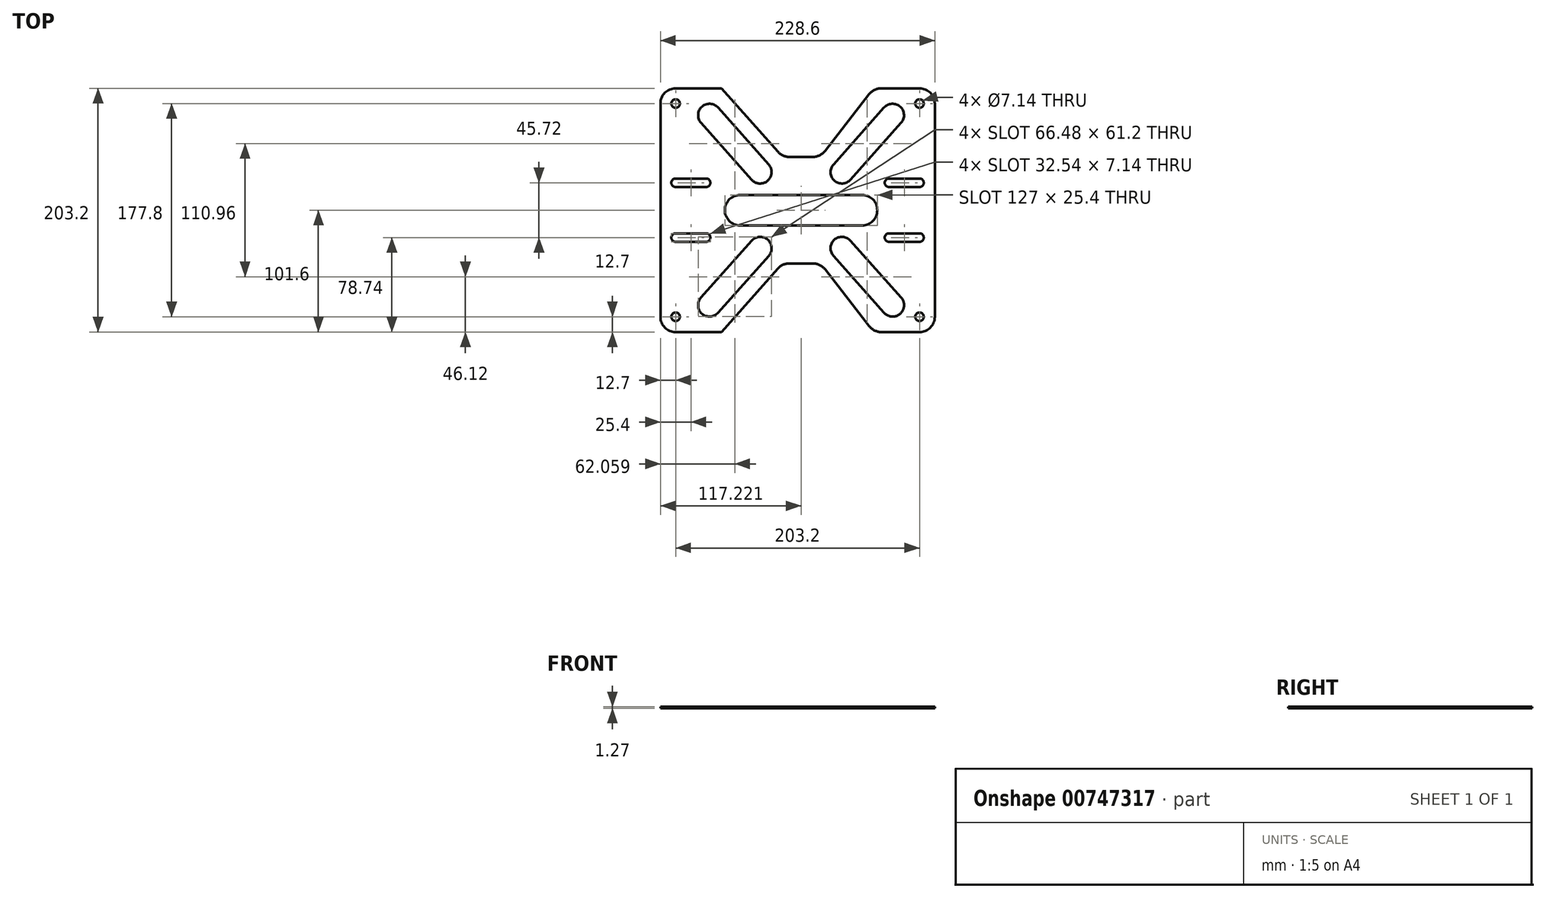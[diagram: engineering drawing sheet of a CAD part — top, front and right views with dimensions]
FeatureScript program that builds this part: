
annotation { "Feature Type Name" : "Feature", "Feature Type Description" : "" }
export const myFeature = defineFeature(function(context is Context, id is Id, definition is map)
    precondition{}
    {
        {
            var Q0;
            Q0=qCreatedBy(makeId("Top.planeOp"),FACE);
            var sketch = newSketch(context, id + "F0", { "sketchPlane" : qUnion([Q0])});
            skLineSegment(sketch, "E0.bottom", {"start": v(0, 0) * mm, "end": v(228.6, 0) * mm});
            skLineSegment(sketch, "E0.top", {"start": v(0, 203.2) * mm, "end": v(228.6, 203.2) * mm});
            skLineSegment(sketch, "E0.left", {"start": v(0, 0) * mm, "end": v(0, 203.2) * mm});
            skLineSegment(sketch, "E0.right", {"start": v(228.6, 0) * mm, "end": v(228.6, 203.2) * mm});
            skSolve(sketch);
        }
        {
            var Q0;
            Q0 = qSketchRegion(id + "F0", true);
            extrude(context, id + "F1", {"entities" : qUnion([Q0]), "depth" : 1.27 * mm, "offsetDistance" : 25.4 * mm});
        }
        {
            var Q0;
            Q0=makeQuery(id+"F1.opExtrude","CAP_FACE",FACE,{"disambiguationData":[OSD([sQuery(id+"F0.wireOp",EDGE,"E0.bottom"),sQuery(id+"F0.wireOp",EDGE,"E0.top"),sQuery(id+"F0.wireOp",EDGE,"E0.left"),sQuery(id+"F0.wireOp",EDGE,"E0.right")])],"isStart":false});
            var sketch = newSketch(context, id + "F2", { "sketchPlane" : qUnion([Q0])});
            skLineSegment(sketch, "E1", {"start": v(12.7, 128.03) * mm, "end": v(38.1, 128.03) * mm});
            skLineSegment(sketch, "E2", {"start": v(12.7, 120.9) * mm, "end": v(38.1, 120.9) * mm});
            skArc(sketch, "E3", {"start": v(12.7, 128.03) * mm, "mid": v(9.13, 124.46) * mm, "end": v(12.7, 120.9) * mm});
            skArc(sketch, "E4", {"start": v(38.1, 128.03) * mm, "mid": v(41.67, 124.46) * mm, "end": v(38.1, 120.9) * mm});
            skLineSegment(sketch, "E5", {"start": v(114.3, 203.2) * mm, "end": v(114.3, 0) * mm, "construction": true});
            skLineSegment(sketch, "E6", {"start": v(0, 101.6) * mm, "end": v(228.6, 101.6) * mm, "construction": true});
            skArc(sketch, "E7.MirrorCS", {"start": v(190.5, 128.03) * mm, "mid": v(186.93, 124.46) * mm, "end": v(190.5, 120.9) * mm});
            skLineSegment(sketch, "E8.MirrorCS", {"start": v(215.9, 120.9) * mm, "end": v(190.5, 120.9) * mm});
            skArc(sketch, "E9.MirrorCS", {"start": v(215.9, 128.03) * mm, "mid": v(219.47, 124.46) * mm, "end": v(215.9, 120.9) * mm});
            skLineSegment(sketch, "E10.MirrorCS", {"start": v(215.9, 128.03) * mm, "end": v(190.5, 128.03) * mm});
            skLineSegment(sketch, "E11.MirrorCS", {"start": v(12.7, 82.3) * mm, "end": v(38.1, 82.3) * mm});
            skLineSegment(sketch, "E12.MirrorCS", {"start": v(12.7, 75.17) * mm, "end": v(38.1, 75.17) * mm});
            skArc(sketch, "E13.MirrorCS", {"start": v(12.7, 75.17) * mm, "mid": v(9.13, 78.74) * mm, "end": v(12.7, 82.3) * mm});
            skArc(sketch, "E14.MirrorCS", {"start": v(38.1, 75.17) * mm, "mid": v(41.67, 78.74) * mm, "end": v(38.1, 82.3) * mm});
            skArc(sketch, "E15.MirrorCS", {"start": v(190.5, 75.17) * mm, "mid": v(186.93, 78.74) * mm, "end": v(190.5, 82.3) * mm});
            skArc(sketch, "E16.MirrorCS", {"start": v(215.9, 75.17) * mm, "mid": v(219.47, 78.74) * mm, "end": v(215.9, 82.3) * mm});
            skLineSegment(sketch, "E17.MirrorCS", {"start": v(215.9, 75.17) * mm, "end": v(190.5, 75.17) * mm});
            skLineSegment(sketch, "E18.MirrorCS", {"start": v(215.9, 82.3) * mm, "end": v(190.5, 82.3) * mm});
            skCircle(sketch, "E19", {"center": v(12.7, 190.5) * mm, "radius": 3.57 * mm});
            skCircle(sketch, "E20.MirrorC", {"center": v(215.9, 190.5) * mm, "radius": 3.57 * mm});
            skCircle(sketch, "E21.MirrorC", {"center": v(12.7, 12.7) * mm, "radius": 3.57 * mm});
            skCircle(sketch, "E22.MirrorC", {"center": v(215.9, 12.7) * mm, "radius": 3.57 * mm});
            skSolve(sketch);
        }
        {
            var Q0;
            Q0 = qSketchRegion(id + "F2", true);
            extrude(context, id + "F3", {"entities" : qUnion([Q0]), "operationType" : NewBodyOperationType.REMOVE, "endBound" : BoundingType.THROUGH_ALL, "oppositeDirection" : true, "depth" : 25.4 * mm, "offsetDistance" : 25.4 * mm});
        }
        {
            var Q0;
            Q0=makeQuery(id+"F1.opExtrude","CAP_FACE",FACE,{"disambiguationData":[OSD([sQuery(id+"F0.wireOp",EDGE,"E0.bottom"),sQuery(id+"F0.wireOp",EDGE,"E0.top"),sQuery(id+"F0.wireOp",EDGE,"E0.left"),sQuery(id+"F0.wireOp",EDGE,"E0.right")])],"isStart":false});
            var sketch = newSketch(context, id + "F4", { "sketchPlane" : qUnion([Q0])});
            skLineSegment(sketch, "E23", {"start": v(101.6, 146.05) * mm, "end": v(133.35, 146.05) * mm});
            skLineSegment(sketch, "E24", {"start": v(0, 101.6) * mm, "end": v(228.6, 101.6) * mm, "construction": true});
            skLineSegment(sketch, "E25", {"start": v(101.6, 146.05) * mm, "end": v(50.8, 203.2) * mm});
            skLineSegment(sketch, "E26", {"start": v(133.35, 146.05) * mm, "end": v(177.8, 203.2) * mm});
            skLineSegment(sketch, "E27", {"start": v(50.8, 203.2) * mm, "end": v(177.8, 203.2) * mm});
            skLineSegment(sketch, "E28.MirrorCS", {"start": v(101.6, 57.15) * mm, "end": v(133.35, 57.15) * mm});
            skLineSegment(sketch, "E29.MirrorCS", {"start": v(101.6, 57.15) * mm, "end": v(50.8, 0) * mm});
            skLineSegment(sketch, "E30.MirrorCS", {"start": v(50.8, 0) * mm, "end": v(177.8, 0) * mm});
            skLineSegment(sketch, "E31.MirrorCS", {"start": v(133.35, 57.15) * mm, "end": v(177.8, 0) * mm});
            skSolve(sketch);
        }
        {
            var Q0;
            Q0 = qSketchRegion(id + "F4", true);
            extrude(context, id + "F5", {"entities" : qUnion([Q0]), "operationType" : NewBodyOperationType.REMOVE, "oppositeDirection" : true, "depth" : 25.4 * mm, "offsetDistance" : 25.4 * mm});
        }
        {
            var Q0;
            Q0=makeQuery(id+"F5.boolean.opBoolean","COPY",EDGE,{"derivedFrom":makeQuery(id+"F5.opExtrude","SWEPT_EDGE",EDGE,{"disambiguationData":[OSD([sQuery(id+"F0.wireOp",EDGE,"E0.bottom"),sQuery(id+"F4.wireOp",EDGE,"E29.MirrorCS"),sQuery(id+"F4.wireOp",EDGE,"E30.MirrorCS")])]})});
            var Q1;
            Q1=makeQuery(id+"F5.boolean.opBoolean","COPY",EDGE,{"derivedFrom":makeQuery(id+"F5.opExtrude","SWEPT_EDGE",EDGE,{"disambiguationData":[OSD([sQuery(id+"F4.wireOp",EDGE,"E28.MirrorCS"),sQuery(id+"F4.wireOp",EDGE,"E29.MirrorCS")])]})});
            var Q2;
            Q2=makeQuery(id+"F1.opExtrude","SWEPT_EDGE",EDGE,{"disambiguationData":[OSD([sQuery(id+"F0.wireOp",EDGE,"E0.bottom"),sQuery(id+"F0.wireOp",EDGE,"E0.left")])]});
            var Q3;
            Q3=makeQuery(id+"F5.boolean.opBoolean","COPY",EDGE,{"derivedFrom":makeQuery(id+"F5.opExtrude","SWEPT_EDGE",EDGE,{"disambiguationData":[OSD([sQuery(id+"F4.wireOp",EDGE,"E28.MirrorCS"),sQuery(id+"F4.wireOp",EDGE,"E31.MirrorCS")])]})});
            var Q4;
            Q4=makeQuery(id+"F5.boolean.opBoolean","COPY",EDGE,{"derivedFrom":makeQuery(id+"F5.opExtrude","SWEPT_EDGE",EDGE,{"disambiguationData":[OSD([sQuery(id+"F0.wireOp",EDGE,"E0.bottom"),sQuery(id+"F4.wireOp",EDGE,"E30.MirrorCS"),sQuery(id+"F4.wireOp",EDGE,"E31.MirrorCS")])]})});
            var Q5;
            Q5=makeQuery(id+"F1.opExtrude","SWEPT_EDGE",EDGE,{"disambiguationData":[OSD([sQuery(id+"F0.wireOp",EDGE,"E0.bottom"),sQuery(id+"F0.wireOp",EDGE,"E0.right")])]});
            var Q6;
            Q6=makeQuery(id+"F1.opExtrude","SWEPT_EDGE",EDGE,{"disambiguationData":[OSD([sQuery(id+"F0.wireOp",EDGE,"E0.top"),sQuery(id+"F0.wireOp",EDGE,"E0.right")])]});
            var Q7;
            Q7=makeQuery(id+"F5.boolean.opBoolean","COPY",EDGE,{"derivedFrom":makeQuery(id+"F5.opExtrude","SWEPT_EDGE",EDGE,{"disambiguationData":[OSD([sQuery(id+"F0.wireOp",EDGE,"E0.top"),sQuery(id+"F4.wireOp",EDGE,"E26"),sQuery(id+"F4.wireOp",EDGE,"E27")])]})});
            var Q8;
            Q8=makeQuery(id+"F5.boolean.opBoolean","COPY",EDGE,{"derivedFrom":makeQuery(id+"F5.opExtrude","SWEPT_EDGE",EDGE,{"disambiguationData":[OSD([sQuery(id+"F4.wireOp",EDGE,"E23"),sQuery(id+"F4.wireOp",EDGE,"E26")])]})});
            var Q9;
            Q9=makeQuery(id+"F5.boolean.opBoolean","COPY",EDGE,{"derivedFrom":makeQuery(id+"F5.opExtrude","SWEPT_EDGE",EDGE,{"disambiguationData":[OSD([sQuery(id+"F4.wireOp",EDGE,"E23"),sQuery(id+"F4.wireOp",EDGE,"E25")])]})});
            var Q10;
            Q10=makeQuery(id+"F5.boolean.opBoolean","COPY",EDGE,{"derivedFrom":makeQuery(id+"F5.opExtrude","SWEPT_EDGE",EDGE,{"disambiguationData":[OSD([sQuery(id+"F0.wireOp",EDGE,"E0.top"),sQuery(id+"F4.wireOp",EDGE,"E25"),sQuery(id+"F4.wireOp",EDGE,"E27")])]})});
            var Q11;
            Q11=makeQuery(id+"F1.opExtrude","SWEPT_EDGE",EDGE,{"disambiguationData":[OSD([sQuery(id+"F0.wireOp",EDGE,"E0.top"),sQuery(id+"F0.wireOp",EDGE,"E0.left")])]});
            fillet(context, id + "F6", {"entities" : qUnion([Q0, Q1, Q2, Q3, Q4, Q5, Q6, Q7, Q8, Q9, Q10, Q11]), "radius" : 12.7 * mm, "tangentPropagation" : true, "allowEdgeOverflow" : false});
        }
        {
            var Q0;
            Q0=makeQuery(id+"F1.opExtrude","CAP_FACE",FACE,{"disambiguationData":[OSD([sQuery(id+"F0.wireOp",EDGE,"E0.bottom"),sQuery(id+"F0.wireOp",EDGE,"E0.top"),sQuery(id+"F0.wireOp",EDGE,"E0.left"),sQuery(id+"F0.wireOp",EDGE,"E0.right")])],"isStart":false});
            var sketch = newSketch(context, id + "F7", { "sketchPlane" : qUnion([Q0])});
            skLineSegment(sketch, "E32", {"start": v(0, 101.6) * mm, "end": v(228.6, 101.6) * mm, "construction": true});
            skLineSegment(sketch, "E33", {"start": v(117.22, 146.05) * mm, "end": v(117.22, 57.15) * mm, "construction": true});
            skLineSegment(sketch, "E34", {"start": v(48.08, 187.14) * mm, "end": v(90.27, 139.68) * mm});
            skLineSegment(sketch, "E35", {"start": v(76.03, 127.02) * mm, "end": v(33.85, 174.48) * mm});
            skArc(sketch, "E36", {"start": v(76.03, 127.02) * mm, "mid": v(89.48, 126.23) * mm, "end": v(90.27, 139.68) * mm});
            skArc(sketch, "E37", {"start": v(48.08, 187.14) * mm, "mid": v(34.64, 187.93) * mm, "end": v(33.85, 174.48) * mm});
            skLineSegment(sketch, "E38.MirrorCS", {"start": v(158.4, 127.02) * mm, "end": v(200.6, 174.48) * mm});
            skArc(sketch, "E39.MirrorCS", {"start": v(186.36, 187.14) * mm, "mid": v(199.8, 187.93) * mm, "end": v(200.6, 174.48) * mm});
            skLineSegment(sketch, "E40.MirrorCS", {"start": v(186.36, 187.14) * mm, "end": v(144.17, 139.68) * mm});
            skArc(sketch, "E41.MirrorCS", {"start": v(158.4, 127.02) * mm, "mid": v(144.96, 126.23) * mm, "end": v(144.17, 139.68) * mm});
            skArc(sketch, "E42.MirrorCS", {"start": v(76.03, 76.18) * mm, "mid": v(89.48, 76.97) * mm, "end": v(90.27, 63.52) * mm});
            skLineSegment(sketch, "E43.MirrorCS", {"start": v(48.08, 16.06) * mm, "end": v(90.27, 63.52) * mm});
            skArc(sketch, "E44.MirrorCS", {"start": v(48.08, 16.06) * mm, "mid": v(34.64, 15.27) * mm, "end": v(33.85, 28.72) * mm});
            skLineSegment(sketch, "E45.MirrorCS", {"start": v(76.03, 76.18) * mm, "end": v(33.85, 28.72) * mm});
            skLineSegment(sketch, "E46.MirrorCS", {"start": v(158.4, 76.18) * mm, "end": v(200.6, 28.72) * mm});
            skLineSegment(sketch, "E47.MirrorCS", {"start": v(186.36, 16.06) * mm, "end": v(144.17, 63.52) * mm});
            skArc(sketch, "E48.MirrorCS", {"start": v(158.4, 76.18) * mm, "mid": v(144.96, 76.97) * mm, "end": v(144.17, 63.52) * mm});
            skArc(sketch, "E49.MirrorCS", {"start": v(186.36, 16.06) * mm, "mid": v(199.8, 15.27) * mm, "end": v(200.6, 28.72) * mm});
            skLineSegment(sketch, "E50", {"start": v(66.42, 88.9) * mm, "end": v(117.22, 88.9) * mm});
            skLineSegment(sketch, "E51.MirrorCS", {"start": v(66.42, 114.3) * mm, "end": v(117.22, 114.3) * mm});
            skLineSegment(sketch, "E52.MirrorCS", {"start": v(168.02, 114.3) * mm, "end": v(117.22, 114.3) * mm});
            skLineSegment(sketch, "E53.MirrorCS", {"start": v(168.02, 88.9) * mm, "end": v(117.22, 88.9) * mm});
            skArc(sketch, "E54", {"start": v(66.42, 88.9) * mm, "mid": v(53.72, 101.6) * mm, "end": v(66.42, 114.3) * mm});
            skArc(sketch, "E55.MirrorCS", {"start": v(168.02, 88.9) * mm, "mid": v(180.72, 101.6) * mm, "end": v(168.02, 114.3) * mm});
            skSolve(sketch);
        }
        {
            var Q0;
            Q0 = qSketchRegion(id + "F7", true);
            extrude(context, id + "F8", {"entities" : qUnion([Q0]), "operationType" : NewBodyOperationType.REMOVE, "oppositeDirection" : true, "depth" : 25.4 * mm, "offsetDistance" : 25.4 * mm});
        }
    });
